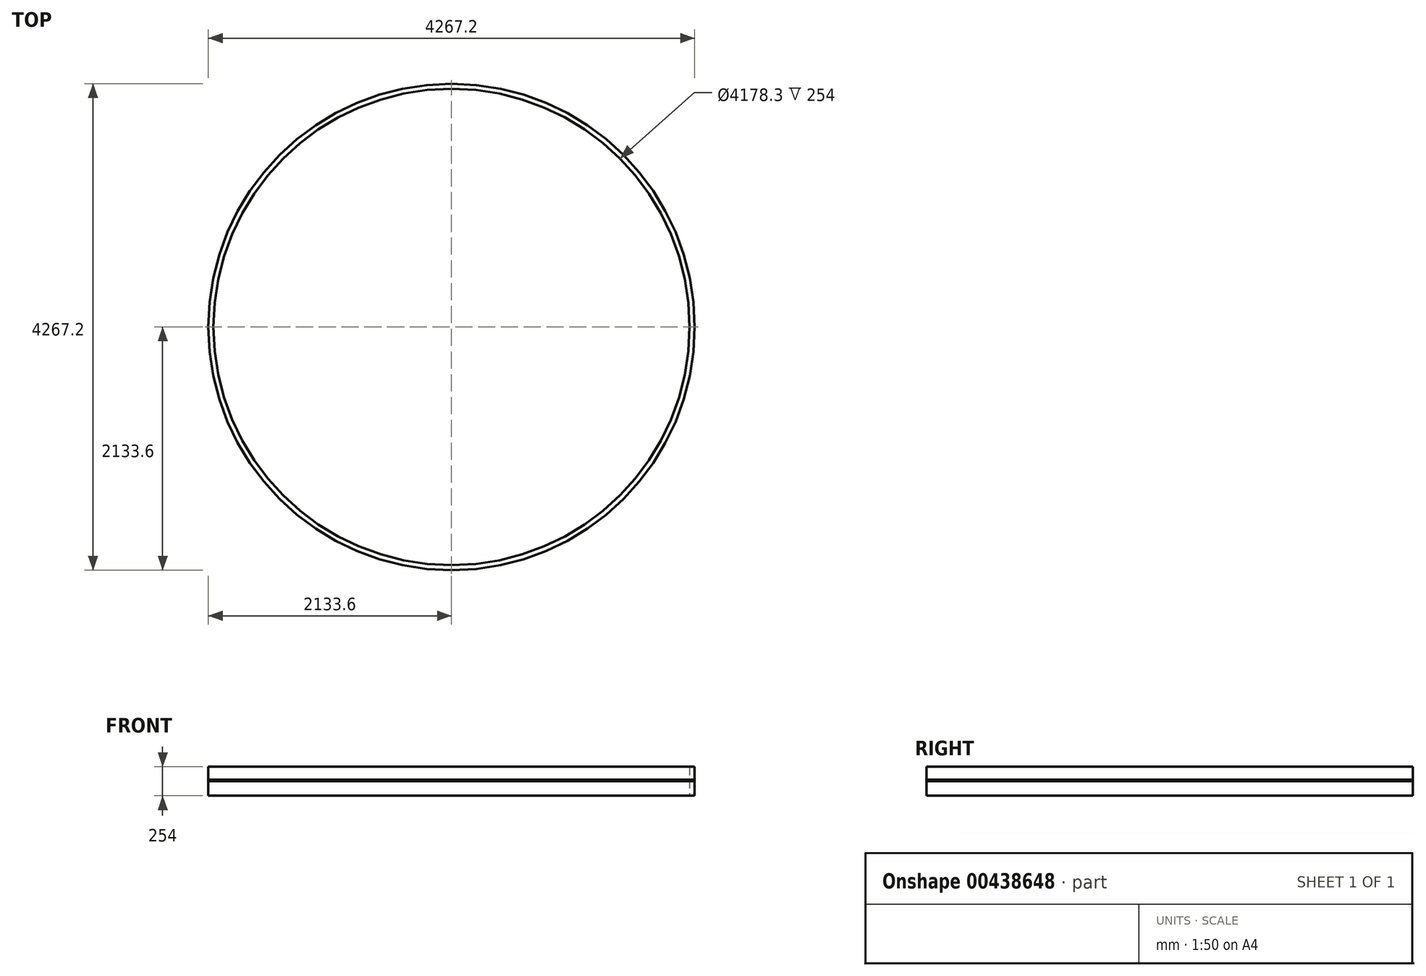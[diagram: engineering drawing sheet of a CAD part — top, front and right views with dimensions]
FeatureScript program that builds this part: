
annotation { "Feature Type Name" : "Feature", "Feature Type Description" : "" }
export const myFeature = defineFeature(function(context is Context, id is Id, definition is map)
    precondition{}
    {
        {
            var Q0;
            Q0=qCreatedBy(makeId("Top.planeOp"),FACE);
            var sketch = newSketch(context, id + "F0", { "sketchPlane" : qUnion([Q0])});
            skCircle(sketch, "E0", {"center": v(0, 0) * mm, "radius": 2133.6 * mm});
            skCircle(sketch, "E1", {"center": v(0, 0) * mm, "radius": 2089.15 * mm});
            skLineSegment(sketch, "E2", {"start": v(0, 0) * mm, "end": v(2571.64, 0) * mm});
            skLineSegment(sketch, "E3", {"start": v(0, 0) * mm, "end": v(-2406.12, 0) * mm});
            skLineSegment(sketch, "E4", {"start": v(0, 0) * mm, "end": v(0, 2379.22) * mm});
            skLineSegment(sketch, "E5", {"start": v(0, 0) * mm, "end": v(-1224.23, 2120.43) * mm});
            skLineSegment(sketch, "E6", {"start": v(0, 0) * mm, "end": v(-2152.78, 1242.9) * mm});
            skLineSegment(sketch, "E7", {"start": v(0, 0) * mm, "end": v(1178.2, 2040.7) * mm});
            skLineSegment(sketch, "E8", {"start": v(0, 0) * mm, "end": v(2048.47, 1182.68) * mm});
            skSolve(sketch);
        }
        {
            var Q0;
            Q0=qCreatedBy(makeId("Top.planeOp"),FACE);
            var sketch = newSketch(context, id + "F1", { "sketchPlane" : qUnion([Q0])});
            skCircle(sketch, "E9", {"center": v(0, 0) * mm, "radius": 2133.6 * mm});
            skSolve(sketch);
        }
        {
            var Q0;
            Q0=makeQuery(id+"F1.imprint","IMPRINT",FACE,{"disambiguationData":[TD([[makeQuery(id+"F1.imprint","IMPRINT",EDGE,{"derivedFrom":sQuery(id+"F1.wireOp",EDGE,"E9")}),1.0]])]});
            var Q1;
            Q1=sQuery(id+"F0.wireOp",EDGE,"E0");
            extrude(context, id + "F2", {"entities" : qUnion([Q0]), "surfaceEntities" : qUnion([Q1]), "depth" : 12.7 * mm});
        }
        {
            var Q0;
            Q0 = qSketchRegion(id + "F0", true);
            var Q1;
            Q1=sQuery(id+"F0.wireOp",EDGE,"E1");
            extrude(context, id + "F3", {"entities" : qUnion([Q0]), "surfaceEntities" : qUnion([Q1]), "endBound" : BoundingType.SYMMETRIC, "depth" : 254 * mm});
        }
    });
